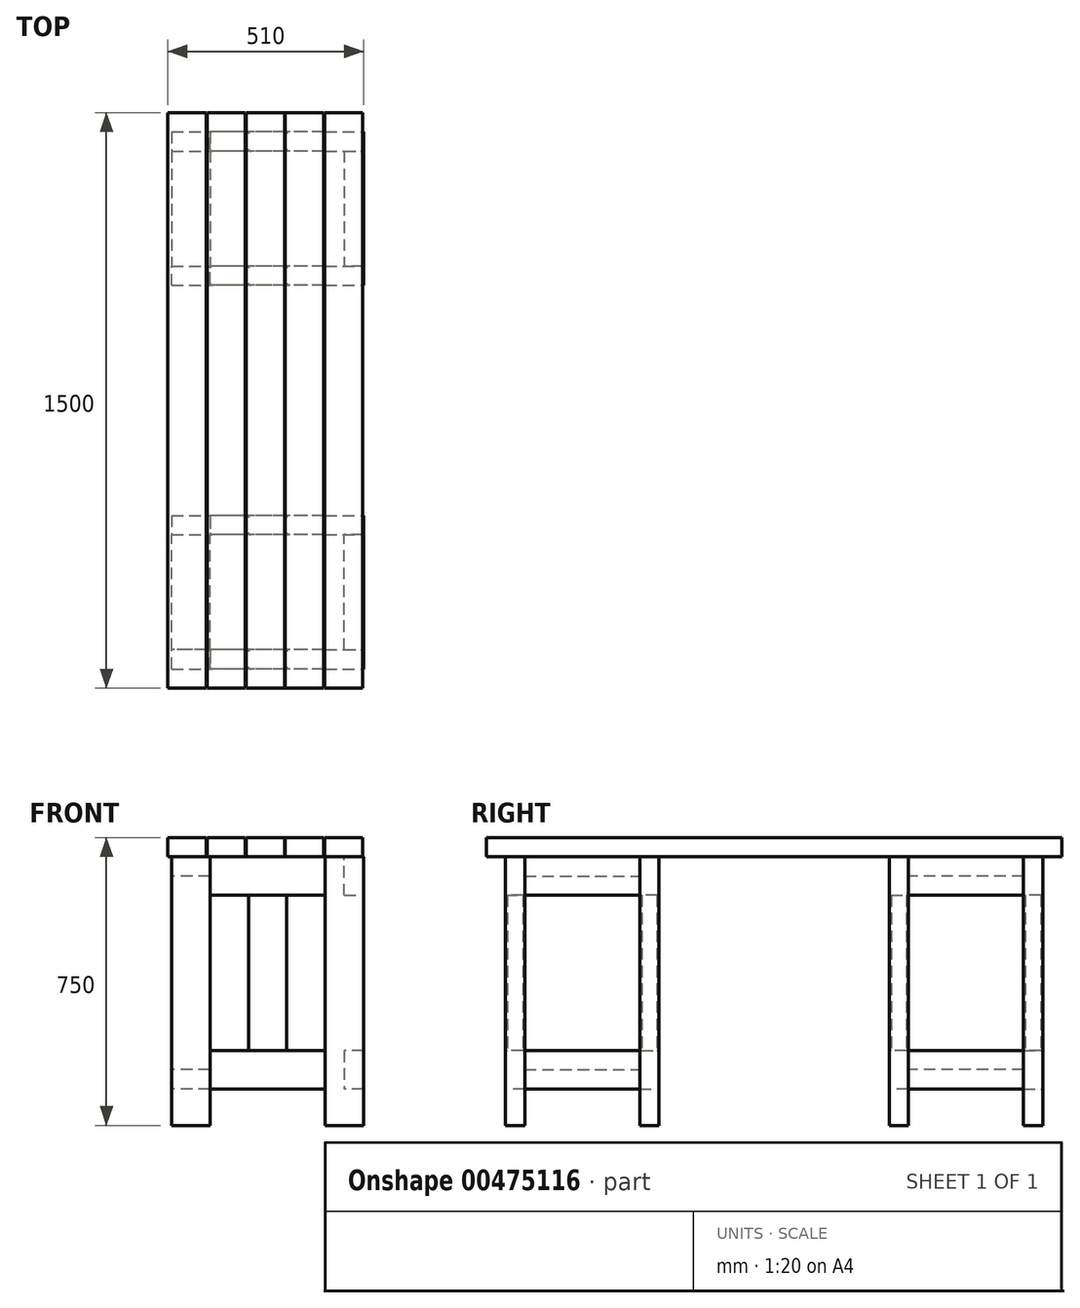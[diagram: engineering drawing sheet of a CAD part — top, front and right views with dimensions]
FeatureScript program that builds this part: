
annotation { "Feature Type Name" : "Feature", "Feature Type Description" : "" }
export const myFeature = defineFeature(function(context is Context, id is Id, definition is map)
    precondition{}
    {
        {
            var Q0;
            Q0=qCreatedBy(makeId("Top.planeOp"),FACE);
            var sketch = newSketch(context, id + "F0", { "sketchPlane" : qUnion([Q0])});
            skLineSegment(sketch, "E0.bottom", {"start": v(-98.78, -63.47) * mm, "end": v(1.22, -63.47) * mm});
            skLineSegment(sketch, "E0.top", {"start": v(-98.78, -13.47) * mm, "end": v(1.22, -13.47) * mm});
            skLineSegment(sketch, "E0.left", {"start": v(-98.78, -63.47) * mm, "end": v(-98.78, -13.47) * mm});
            skLineSegment(sketch, "E0.right", {"start": v(1.22, -63.47) * mm, "end": v(1.22, -13.47) * mm});
            skLineSegment(sketch, "E1.bottom", {"start": v(301.22, -63.47) * mm, "end": v(401.22, -63.47) * mm});
            skLineSegment(sketch, "E1.top", {"start": v(301.22, -13.47) * mm, "end": v(401.22, -13.47) * mm});
            skLineSegment(sketch, "E1.left", {"start": v(301.22, -63.47) * mm, "end": v(301.22, -13.47) * mm});
            skLineSegment(sketch, "E1.right", {"start": v(401.22, -63.47) * mm, "end": v(401.22, -13.47) * mm});
            skLineSegment(sketch, "E2.bottom", {"start": v(-98.78, 336.53) * mm, "end": v(1.22, 336.53) * mm});
            skLineSegment(sketch, "E2.top", {"start": v(-98.78, 286.53) * mm, "end": v(1.22, 286.53) * mm});
            skLineSegment(sketch, "E2.left", {"start": v(-98.78, 336.53) * mm, "end": v(-98.78, 286.53) * mm});
            skLineSegment(sketch, "E2.right", {"start": v(1.22, 336.53) * mm, "end": v(1.22, 286.53) * mm});
            skLineSegment(sketch, "E3.bottom", {"start": v(301.22, 336.53) * mm, "end": v(401.22, 336.53) * mm});
            skLineSegment(sketch, "E3.top", {"start": v(301.22, 286.53) * mm, "end": v(401.22, 286.53) * mm});
            skLineSegment(sketch, "E3.left", {"start": v(301.22, 336.53) * mm, "end": v(301.22, 286.53) * mm});
            skLineSegment(sketch, "E3.right", {"start": v(401.22, 336.53) * mm, "end": v(401.22, 286.53) * mm});
            skSolve(sketch);
        }
        {
            var Q0;
            Q0 = qSketchRegion(id + "F0", true);
            extrude(context, id + "F1", {"entities" : qUnion([Q0]), "depth" : 700 * mm, "offsetDistance" : 25 * mm});
        }
        {
            var Q0;
            Q0=makeQuery(id+"F1.opExtrude","SWEPT_FACE",FACE,{"disambiguationData":[OSD([sQuery(id+"F0.wireOp",EDGE,"E0.right")])]});
            var sketch = newSketch(context, id + "F2", { "sketchPlane" : qUnion([Q0])});
            skLineSegment(sketch, "E4.bottom", {"start": v(-13.47, 700) * mm, "end": v(-63.47, 700) * mm});
            skLineSegment(sketch, "E4.top", {"start": v(-13.47, 600) * mm, "end": v(-63.47, 600) * mm});
            skLineSegment(sketch, "E4.left", {"start": v(-13.47, 700) * mm, "end": v(-13.47, 600) * mm});
            skLineSegment(sketch, "E4.right", {"start": v(-63.47, 700) * mm, "end": v(-63.47, 600) * mm});
            skLineSegment(sketch, "E5.bottom", {"start": v(-63.47, 95) * mm, "end": v(-13.47, 95) * mm});
            skLineSegment(sketch, "E5.top", {"start": v(-63.47, 195) * mm, "end": v(-13.47, 195) * mm});
            skLineSegment(sketch, "E5.left", {"start": v(-63.47, 95) * mm, "end": v(-63.47, 195) * mm});
            skLineSegment(sketch, "E5.right", {"start": v(-13.47, 95) * mm, "end": v(-13.47, 195) * mm});
            skLineSegment(sketch, "E6.bottom", {"start": v(336.53, 700) * mm, "end": v(286.53, 700) * mm});
            skLineSegment(sketch, "E6.top", {"start": v(336.53, 600) * mm, "end": v(286.53, 600) * mm});
            skLineSegment(sketch, "E6.left", {"start": v(336.53, 700) * mm, "end": v(336.53, 600) * mm});
            skLineSegment(sketch, "E6.right", {"start": v(286.53, 700) * mm, "end": v(286.53, 600) * mm});
            skLineSegment(sketch, "E7.bottom", {"start": v(286.53, 195) * mm, "end": v(336.53, 195) * mm});
            skLineSegment(sketch, "E7.top", {"start": v(286.53, 95) * mm, "end": v(336.53, 95) * mm});
            skLineSegment(sketch, "E7.left", {"start": v(286.53, 195) * mm, "end": v(286.53, 95) * mm});
            skLineSegment(sketch, "E7.right", {"start": v(336.53, 195) * mm, "end": v(336.53, 95) * mm});
            skSolve(sketch);
        }
        {
            var Q0;
            Q0 = qSketchRegion(id + "F2", true);
            extrude(context, id + "F3", {"entities" : qUnion([Q0]), "endBound" : BoundingType.UP_TO_NEXT, "depth" : 25 * mm, "offsetDistance" : 25 * mm});
        }
        {
            var Q0;
            Q0=makeQuery(id+"F1.opExtrude","SWEPT_FACE",FACE,{"disambiguationData":[OSD([sQuery(id+"F0.wireOp",EDGE,"E2.top")])]});
            var sketch = newSketch(context, id + "F4", { "sketchPlane" : qUnion([Q0])});
            skLineSegment(sketch, "E8.bottom", {"start": v(-98.78, 700) * mm, "end": v(1.22, 700) * mm});
            skLineSegment(sketch, "E8.top", {"start": v(-98.78, 650) * mm, "end": v(1.22, 650) * mm});
            skLineSegment(sketch, "E8.left", {"start": v(-98.78, 700) * mm, "end": v(-98.78, 650) * mm});
            skLineSegment(sketch, "E8.right", {"start": v(1.22, 700) * mm, "end": v(1.22, 650) * mm});
            skLineSegment(sketch, "E9.bottom", {"start": v(-98.78, 95) * mm, "end": v(1.22, 95) * mm});
            skLineSegment(sketch, "E9.top", {"start": v(-98.78, 145) * mm, "end": v(1.22, 145) * mm});
            skLineSegment(sketch, "E9.left", {"start": v(-98.78, 95) * mm, "end": v(-98.78, 145) * mm});
            skLineSegment(sketch, "E9.right", {"start": v(1.22, 95) * mm, "end": v(1.22, 145) * mm});
            skLineSegment(sketch, "E10.bottom", {"start": v(401.22, 700) * mm, "end": v(351.22, 700) * mm});
            skLineSegment(sketch, "E10.top", {"start": v(401.22, 600) * mm, "end": v(351.22, 600) * mm});
            skLineSegment(sketch, "E10.left", {"start": v(401.22, 700) * mm, "end": v(401.22, 600) * mm});
            skLineSegment(sketch, "E10.right", {"start": v(351.22, 700) * mm, "end": v(351.22, 600) * mm});
            skLineSegment(sketch, "E11.bottom", {"start": v(351.22, 95) * mm, "end": v(401.22, 95) * mm});
            skLineSegment(sketch, "E11.top", {"start": v(351.22, 195) * mm, "end": v(401.22, 195) * mm});
            skLineSegment(sketch, "E11.left", {"start": v(351.22, 95) * mm, "end": v(351.22, 195) * mm});
            skLineSegment(sketch, "E11.right", {"start": v(401.22, 95) * mm, "end": v(401.22, 195) * mm});
            skSolve(sketch);
        }
        {
            var Q0;
            Q0 = qSketchRegion(id + "F4", true);
            extrude(context, id + "F5", {"entities" : qUnion([Q0]), "endBound" : BoundingType.UP_TO_NEXT, "depth" : 25 * mm, "offsetDistance" : 25 * mm});
        }
        {
            var Q0;
            Q0=makeQuery(id+"F3.opExtrude","SWEPT_FACE",FACE,{"disambiguationData":[OSD([sQuery(id+"F2.wireOp",EDGE,"E5.top")])]});
            var sketch = newSketch(context, id + "F6", { "sketchPlane" : qUnion([Q0])});
            skLineSegment(sketch, "E12.bottom", {"start": v(6.22, -13.47) * mm, "end": v(96.22, -13.47) * mm});
            skLineSegment(sketch, "E12.top", {"start": v(6.22, -63.47) * mm, "end": v(96.22, -63.47) * mm});
            skLineSegment(sketch, "E12.left", {"start": v(1.22, -18.47) * mm, "end": v(1.22, -58.47) * mm});
            skLineSegment(sketch, "E12.right", {"start": v(101.22, -13.47) * mm, "end": v(101.22, -63.47) * mm});
            skLineSegment(sketch, "E13.bottom", {"start": v(106.22, -13.47) * mm, "end": v(196.22, -13.47) * mm});
            skLineSegment(sketch, "E13.top", {"start": v(106.22, -63.47) * mm, "end": v(196.22, -63.47) * mm});
            skLineSegment(sketch, "E13.left", {"start": v(101.22, -18.47) * mm, "end": v(101.22, -58.47) * mm});
            skLineSegment(sketch, "E13.right", {"start": v(201.22, -13.47) * mm, "end": v(201.22, -63.47) * mm});
            skLineSegment(sketch, "E14.bottom", {"start": v(206.22, -13.47) * mm, "end": v(296.22, -13.47) * mm});
            skLineSegment(sketch, "E14.top", {"start": v(206.22, -63.47) * mm, "end": v(296.22, -63.47) * mm});
            skLineSegment(sketch, "E14.left", {"start": v(201.22, -18.47) * mm, "end": v(201.22, -58.47) * mm});
            skLineSegment(sketch, "E14.right", {"start": v(301.22, -18.47) * mm, "end": v(301.22, -58.47) * mm});
            skPoint(sketch, "E15.visualSharp", {"position": v(101.22, -63.47) * mm});
            skArc(sketch, "E15.filletArc", {"start": v(96.22, -63.47) * mm, "mid": v(99.76, -62) * mm, "end": v(101.22, -58.47) * mm});
            skPoint(sketch, "E16.visualSharp", {"position": v(101.22, -13.47) * mm});
            skArc(sketch, "E16.filletArc", {"start": v(101.22, -18.47) * mm, "mid": v(99.76, -14.94) * mm, "end": v(96.22, -13.47) * mm});
            skPoint(sketch, "E17.visualSharp", {"position": v(1.22, -13.47) * mm});
            skArc(sketch, "E17.filletArc", {"start": v(6.22, -13.47) * mm, "mid": v(2.69, -14.94) * mm, "end": v(1.22, -18.47) * mm});
            skPoint(sketch, "E18.visualSharp", {"position": v(1.22, -63.47) * mm});
            skArc(sketch, "E18.filletArc", {"start": v(1.22, -58.47) * mm, "mid": v(2.69, -62) * mm, "end": v(6.22, -63.47) * mm});
            skArc(sketch, "E19.filletArc", {"start": v(106.22, -13.47) * mm, "mid": v(102.69, -14.94) * mm, "end": v(101.22, -18.47) * mm});
            skArc(sketch, "E20.filletArc", {"start": v(101.22, -58.47) * mm, "mid": v(102.69, -62) * mm, "end": v(106.22, -63.47) * mm});
            skPoint(sketch, "E21.visualSharp", {"position": v(201.22, -63.47) * mm});
            skArc(sketch, "E21.filletArc", {"start": v(196.22, -63.47) * mm, "mid": v(199.76, -62) * mm, "end": v(201.22, -58.47) * mm});
            skPoint(sketch, "E22.visualSharp", {"position": v(201.22, -13.47) * mm});
            skArc(sketch, "E22.filletArc", {"start": v(201.22, -18.47) * mm, "mid": v(199.76, -14.94) * mm, "end": v(196.22, -13.47) * mm});
            skArc(sketch, "E23.filletArc", {"start": v(206.22, -13.47) * mm, "mid": v(202.69, -14.94) * mm, "end": v(201.22, -18.47) * mm});
            skArc(sketch, "E24.filletArc", {"start": v(201.22, -58.47) * mm, "mid": v(202.69, -62) * mm, "end": v(206.22, -63.47) * mm});
            skPoint(sketch, "E25.visualSharp", {"position": v(301.22, -13.47) * mm});
            skArc(sketch, "E25.filletArc", {"start": v(301.22, -18.47) * mm, "mid": v(299.76, -14.94) * mm, "end": v(296.22, -13.47) * mm});
            skPoint(sketch, "E26.visualSharp", {"position": v(301.22, -63.47) * mm});
            skArc(sketch, "E26.filletArc", {"start": v(296.22, -63.47) * mm, "mid": v(299.76, -62) * mm, "end": v(301.22, -58.47) * mm});
            skSolve(sketch);
        }
        {
            var Q0;
            Q0=makeQuery(id+"F6.imprint","IMPRINT",FACE,{"disambiguationData":[TD([[makeQuery(id+"F6.imprint","IMPRINT",EDGE,{"derivedFrom":sQuery(id+"F6.wireOp",EDGE,"E14.bottom")}),1.0]])]});
            var Q1;
            Q1=makeQuery(id+"F6.imprint","IMPRINT",FACE,{"disambiguationData":[TD([[makeQuery(id+"F6.imprint","IMPRINT",EDGE,{"derivedFrom":sQuery(id+"F6.wireOp",EDGE,"E13.bottom")}),1.0]])]});
            var Q2;
            Q2=makeQuery(id+"F6.imprint","IMPRINT",FACE,{"disambiguationData":[TD([[makeQuery(id+"F6.imprint","IMPRINT",EDGE,{"derivedFrom":sQuery(id+"F6.wireOp",EDGE,"E12.bottom")}),1.0]])]});
            extrude(context, id + "F7", {"entities" : qUnion([Q0, Q1, Q2]), "endBound" : BoundingType.UP_TO_NEXT, "depth" : 25 * mm, "offsetDistance" : 25 * mm});
        }
        {
            var Q0;
            Q0=makeQuery(id+"F3.opExtrude","SWEPT_FACE",FACE,{"disambiguationData":[OSD([sQuery(id+"F2.wireOp",EDGE,"E7.bottom")])]});
            var sketch = newSketch(context, id + "F8", { "sketchPlane" : qUnion([Q0])});
            skLineSegment(sketch, "E27.bottom", {"start": v(296.22, 336.53) * mm, "end": v(206.22, 336.53) * mm});
            skLineSegment(sketch, "E27.top", {"start": v(296.22, 286.53) * mm, "end": v(206.22, 286.53) * mm});
            skLineSegment(sketch, "E27.left", {"start": v(301.22, 331.53) * mm, "end": v(301.22, 291.53) * mm});
            skLineSegment(sketch, "E27.right", {"start": v(201.22, 336.53) * mm, "end": v(201.22, 286.53) * mm});
            skLineSegment(sketch, "E28.bottom", {"start": v(196.22, 336.53) * mm, "end": v(106.22, 336.53) * mm});
            skLineSegment(sketch, "E28.top", {"start": v(196.22, 286.53) * mm, "end": v(106.22, 286.53) * mm});
            skLineSegment(sketch, "E28.left", {"start": v(201.22, 331.53) * mm, "end": v(201.22, 291.53) * mm});
            skLineSegment(sketch, "E28.right", {"start": v(101.22, 336.53) * mm, "end": v(101.22, 286.53) * mm});
            skLineSegment(sketch, "E29.bottom", {"start": v(96.22, 336.53) * mm, "end": v(6.22, 336.53) * mm});
            skLineSegment(sketch, "E29.top", {"start": v(96.22, 286.53) * mm, "end": v(6.22, 286.53) * mm});
            skLineSegment(sketch, "E29.left", {"start": v(101.22, 331.53) * mm, "end": v(101.22, 291.53) * mm});
            skLineSegment(sketch, "E29.right", {"start": v(1.22, 331.53) * mm, "end": v(1.22, 291.53) * mm});
            skPoint(sketch, "E30.visualSharp", {"position": v(301.22, 286.53) * mm});
            skArc(sketch, "E30.filletArc", {"start": v(296.22, 286.53) * mm, "mid": v(299.76, 288) * mm, "end": v(301.22, 291.53) * mm});
            skPoint(sketch, "E31.visualSharp", {"position": v(301.22, 336.53) * mm});
            skArc(sketch, "E31.filletArc", {"start": v(301.22, 331.53) * mm, "mid": v(299.76, 335.06) * mm, "end": v(296.22, 336.53) * mm});
            skPoint(sketch, "E32.visualSharp", {"position": v(201.22, 336.53) * mm});
            skArc(sketch, "E32.filletArc", {"start": v(206.22, 336.53) * mm, "mid": v(202.69, 335.06) * mm, "end": v(201.22, 331.53) * mm});
            skPoint(sketch, "E33.visualSharp", {"position": v(201.22, 286.53) * mm});
            skArc(sketch, "E33.filletArc", {"start": v(201.22, 291.53) * mm, "mid": v(202.69, 288) * mm, "end": v(206.22, 286.53) * mm});
            skArc(sketch, "E34.filletArc", {"start": v(196.22, 286.53) * mm, "mid": v(199.76, 288) * mm, "end": v(201.22, 291.53) * mm});
            skArc(sketch, "E35.filletArc", {"start": v(201.22, 331.53) * mm, "mid": v(199.76, 335.06) * mm, "end": v(196.22, 336.53) * mm});
            skPoint(sketch, "E36.visualSharp", {"position": v(101.22, 286.53) * mm});
            skArc(sketch, "E36.filletArc", {"start": v(101.22, 291.53) * mm, "mid": v(102.69, 288) * mm, "end": v(106.22, 286.53) * mm});
            skPoint(sketch, "E37.visualSharp", {"position": v(101.22, 336.53) * mm});
            skArc(sketch, "E37.filletArc", {"start": v(106.22, 336.53) * mm, "mid": v(102.69, 335.06) * mm, "end": v(101.22, 331.53) * mm});
            skArc(sketch, "E38.filletArc", {"start": v(101.22, 331.53) * mm, "mid": v(99.76, 335.06) * mm, "end": v(96.22, 336.53) * mm});
            skArc(sketch, "E39.filletArc", {"start": v(96.22, 286.53) * mm, "mid": v(99.76, 288) * mm, "end": v(101.22, 291.53) * mm});
            skPoint(sketch, "E40.visualSharp", {"position": v(1.22, 336.53) * mm});
            skArc(sketch, "E40.filletArc", {"start": v(6.22, 336.53) * mm, "mid": v(2.69, 335.06) * mm, "end": v(1.22, 331.53) * mm});
            skPoint(sketch, "E41.visualSharp", {"position": v(1.22, 286.53) * mm});
            skArc(sketch, "E41.filletArc", {"start": v(1.22, 291.53) * mm, "mid": v(2.69, 288) * mm, "end": v(6.22, 286.53) * mm});
            skSolve(sketch);
        }
        {
            var Q0;
            Q0 = qSketchRegion(id + "F8", true);
            extrude(context, id + "F9", {"entities" : qUnion([Q0]), "endBound" : BoundingType.UP_TO_NEXT, "depth" : 25 * mm, "offsetDistance" : 25 * mm});
        }
        {
            var Q0;
            Q0=makeQuery(id+"F1.opExtrude","CAP_FACE",FACE,{"disambiguationData":[OSD([sQuery(id+"F0.wireOp",EDGE,"E0.bottom"),sQuery(id+"F0.wireOp",EDGE,"E0.top"),sQuery(id+"F0.wireOp",EDGE,"E0.left"),sQuery(id+"F0.wireOp",EDGE,"E0.right")])],"isStart":false});
            var sketch = newSketch(context, id + "F10", { "sketchPlane" : qUnion([Q0])});
            skLineSegment(sketch, "E42.bottom", {"start": v(399.22, -113.47) * mm, "end": v(299.22, -113.47) * mm});
            skLineSegment(sketch, "E42.top", {"start": v(399.22, 1386.53) * mm, "end": v(299.22, 1386.53) * mm});
            skLineSegment(sketch, "E42.left", {"start": v(399.22, -113.47) * mm, "end": v(399.22, 1386.53) * mm});
            skLineSegment(sketch, "E42.right", {"start": v(299.22, -113.47) * mm, "end": v(299.22, 1386.53) * mm});
            skLineSegment(sketch, "E43.bottom", {"start": v(297.22, -113.47) * mm, "end": v(197.22, -113.47) * mm});
            skLineSegment(sketch, "E43.top", {"start": v(297.22, 1386.53) * mm, "end": v(197.22, 1386.53) * mm});
            skLineSegment(sketch, "E43.left", {"start": v(297.22, -113.47) * mm, "end": v(297.22, 1386.53) * mm});
            skLineSegment(sketch, "E43.right", {"start": v(197.22, -113.47) * mm, "end": v(197.22, 1386.53) * mm});
            skLineSegment(sketch, "E44.bottom", {"start": v(195.22, -113.47) * mm, "end": v(95.22, -113.47) * mm});
            skLineSegment(sketch, "E44.top", {"start": v(195.22, 1386.53) * mm, "end": v(95.22, 1386.53) * mm});
            skLineSegment(sketch, "E44.left", {"start": v(195.22, -113.47) * mm, "end": v(195.22, 1386.53) * mm});
            skLineSegment(sketch, "E44.right", {"start": v(95.22, -113.47) * mm, "end": v(95.22, 1386.53) * mm});
            skLineSegment(sketch, "E45.bottom", {"start": v(93.22, -113.47) * mm, "end": v(-6.78, -113.47) * mm});
            skLineSegment(sketch, "E45.top", {"start": v(93.22, 1386.53) * mm, "end": v(-6.78, 1386.53) * mm});
            skLineSegment(sketch, "E45.left", {"start": v(93.22, -113.47) * mm, "end": v(93.22, 1386.53) * mm});
            skLineSegment(sketch, "E45.right", {"start": v(-6.78, -113.47) * mm, "end": v(-6.78, 1386.53) * mm});
            skLineSegment(sketch, "E46.bottom", {"start": v(-8.78, -113.47) * mm, "end": v(-108.78, -113.47) * mm});
            skLineSegment(sketch, "E46.top", {"start": v(-8.78, 1386.53) * mm, "end": v(-108.78, 1386.53) * mm});
            skLineSegment(sketch, "E46.left", {"start": v(-8.78, -113.47) * mm, "end": v(-8.78, 1386.53) * mm});
            skLineSegment(sketch, "E46.right", {"start": v(-108.78, -113.47) * mm, "end": v(-108.78, 1386.53) * mm});
            skSolve(sketch);
        }
        {
            var Q0;
            Q0 = qSketchRegion(id + "F10", true);
            extrude(context, id + "F11", {"entities" : qUnion([Q0]), "depth" : 50 * mm, "offsetDistance" : 25 * mm});
        }
        {
            var Q0;
            Q0=makeQuery(id+"F3.opExtrude","SWEPT_FACE",FACE,{"disambiguationData":[OSD([sQuery(id+"F2.wireOp",EDGE,"E6.left")])]});
            cPlane(context, id + "F12", {"entities" : qUnion([Q0]), "cplaneType" : CPlaneType.OFFSET, "offset" : 300 * mm, "width" : 150 * mm, "height" : 150 * mm});
        }
        {
            var Q0;
            Q0=makeQuery(id+"F3.opExtrude","SWEPT_BODY",BODY,{"disambiguationData":[OSD([sQuery(id+"F2.wireOp",EDGE,"E6.bottom"),sQuery(id+"F2.wireOp",EDGE,"E6.top"),sQuery(id+"F2.wireOp",EDGE,"E6.left"),sQuery(id+"F2.wireOp",EDGE,"E6.right")])]});
            var Q1;
            Q1=makeQuery(id+"F1.opExtrude","SWEPT_BODY",BODY,{"disambiguationData":[OSD([sQuery(id+"F0.wireOp",EDGE,"E2.bottom"),sQuery(id+"F0.wireOp",EDGE,"E2.top"),sQuery(id+"F0.wireOp",EDGE,"E2.left"),sQuery(id+"F0.wireOp",EDGE,"E2.right")])]});
            var Q2;
            Q2=makeQuery(id+"F9.opExtrude","SWEPT_BODY",BODY,{"disambiguationData":[OSD([sQuery(id+"F8.wireOp",EDGE,"E27.bottom"),sQuery(id+"F8.wireOp",EDGE,"E27.top"),sQuery(id+"F8.wireOp",EDGE,"E27.left"),sQuery(id+"F8.wireOp",EDGE,"E28.bottom"),sQuery(id+"F8.wireOp",EDGE,"E28.top"),sQuery(id+"F8.wireOp",EDGE,"E29.bottom"),sQuery(id+"F8.wireOp",EDGE,"E29.top"),sQuery(id+"F8.wireOp",EDGE,"E29.right"),sQuery(id+"F8.wireOp",EDGE,"E30.filletArc"),sQuery(id+"F8.wireOp",EDGE,"E31.filletArc"),sQuery(id+"F8.wireOp",EDGE,"E32.filletArc"),sQuery(id+"F8.wireOp",EDGE,"E33.filletArc"),sQuery(id+"F8.wireOp",EDGE,"E34.filletArc"),sQuery(id+"F8.wireOp",EDGE,"E35.filletArc"),sQuery(id+"F8.wireOp",EDGE,"E36.filletArc"),sQuery(id+"F8.wireOp",EDGE,"E37.filletArc"),sQuery(id+"F8.wireOp",EDGE,"E38.filletArc"),sQuery(id+"F8.wireOp",EDGE,"E39.filletArc"),sQuery(id+"F8.wireOp",EDGE,"E40.filletArc"),sQuery(id+"F8.wireOp",EDGE,"E41.filletArc")])]});
            var Q3;
            Q3=makeQuery(id+"F1.opExtrude","SWEPT_BODY",BODY,{"disambiguationData":[OSD([sQuery(id+"F0.wireOp",EDGE,"E3.bottom"),sQuery(id+"F0.wireOp",EDGE,"E3.top"),sQuery(id+"F0.wireOp",EDGE,"E3.left"),sQuery(id+"F0.wireOp",EDGE,"E3.right")])]});
            var Q4;
            Q4=makeQuery(id+"F3.opExtrude","SWEPT_BODY",BODY,{"disambiguationData":[OSD([sQuery(id+"F2.wireOp",EDGE,"E7.bottom"),sQuery(id+"F2.wireOp",EDGE,"E7.top"),sQuery(id+"F2.wireOp",EDGE,"E7.left"),sQuery(id+"F2.wireOp",EDGE,"E7.right")])]});
            var Q5;
            Q5=makeQuery(id+"F1.opExtrude","SWEPT_BODY",BODY,{"disambiguationData":[OSD([sQuery(id+"F0.wireOp",EDGE,"E0.bottom"),sQuery(id+"F0.wireOp",EDGE,"E0.top"),sQuery(id+"F0.wireOp",EDGE,"E0.left"),sQuery(id+"F0.wireOp",EDGE,"E0.right")])]});
            var Q6;
            Q6=makeQuery(id+"F1.opExtrude","SWEPT_BODY",BODY,{"disambiguationData":[OSD([sQuery(id+"F0.wireOp",EDGE,"E1.bottom"),sQuery(id+"F0.wireOp",EDGE,"E1.top"),sQuery(id+"F0.wireOp",EDGE,"E1.left"),sQuery(id+"F0.wireOp",EDGE,"E1.right")])]});
            var Q7;
            Q7=makeQuery(id+"F3.opExtrude","SWEPT_BODY",BODY,{"disambiguationData":[OSD([sQuery(id+"F2.wireOp",EDGE,"E4.bottom"),sQuery(id+"F2.wireOp",EDGE,"E4.top"),sQuery(id+"F2.wireOp",EDGE,"E4.left"),sQuery(id+"F2.wireOp",EDGE,"E4.right")])]});
            var Q8;
            Q8=makeQuery(id+"F3.opExtrude","SWEPT_BODY",BODY,{"disambiguationData":[OSD([sQuery(id+"F2.wireOp",EDGE,"E5.bottom"),sQuery(id+"F2.wireOp",EDGE,"E5.top"),sQuery(id+"F2.wireOp",EDGE,"E5.left"),sQuery(id+"F2.wireOp",EDGE,"E5.right")])]});
            var Q9;
            Q9=makeQuery(id+"F5.opExtrude","SWEPT_BODY",BODY,{"disambiguationData":[OSD([sQuery(id+"F4.wireOp",EDGE,"E8.bottom"),sQuery(id+"F4.wireOp",EDGE,"E8.top"),sQuery(id+"F4.wireOp",EDGE,"E8.left"),sQuery(id+"F4.wireOp",EDGE,"E8.right")])]});
            var Q10;
            Q10=makeQuery(id+"F5.opExtrude","SWEPT_BODY",BODY,{"disambiguationData":[OSD([sQuery(id+"F4.wireOp",EDGE,"E9.bottom"),sQuery(id+"F4.wireOp",EDGE,"E9.top"),sQuery(id+"F4.wireOp",EDGE,"E9.left"),sQuery(id+"F4.wireOp",EDGE,"E9.right")])]});
            var Q11;
            Q11=makeQuery(id+"F5.opExtrude","SWEPT_BODY",BODY,{"disambiguationData":[OSD([sQuery(id+"F4.wireOp",EDGE,"E10.bottom"),sQuery(id+"F4.wireOp",EDGE,"E10.top"),sQuery(id+"F4.wireOp",EDGE,"E10.left"),sQuery(id+"F4.wireOp",EDGE,"E10.right")])]});
            var Q12;
            Q12=makeQuery(id+"F5.opExtrude","SWEPT_BODY",BODY,{"disambiguationData":[OSD([sQuery(id+"F4.wireOp",EDGE,"E11.bottom"),sQuery(id+"F4.wireOp",EDGE,"E11.top"),sQuery(id+"F4.wireOp",EDGE,"E11.left"),sQuery(id+"F4.wireOp",EDGE,"E11.right")])]});
            var Q13;
            Q13=makeQuery(id+"F7.opExtrude","SWEPT_BODY",BODY,{"disambiguationData":[OSD([sQuery(id+"F6.wireOp",EDGE,"E12.bottom"),sQuery(id+"F6.wireOp",EDGE,"E12.top"),sQuery(id+"F6.wireOp",EDGE,"E12.left"),sQuery(id+"F6.wireOp",EDGE,"E13.bottom"),sQuery(id+"F6.wireOp",EDGE,"E13.top"),sQuery(id+"F6.wireOp",EDGE,"E14.bottom"),sQuery(id+"F6.wireOp",EDGE,"E14.top"),sQuery(id+"F6.wireOp",EDGE,"E14.right"),sQuery(id+"F6.wireOp",EDGE,"E15.filletArc"),sQuery(id+"F6.wireOp",EDGE,"E16.filletArc"),sQuery(id+"F6.wireOp",EDGE,"E17.filletArc"),sQuery(id+"F6.wireOp",EDGE,"E18.filletArc"),sQuery(id+"F6.wireOp",EDGE,"E19.filletArc"),sQuery(id+"F6.wireOp",EDGE,"E20.filletArc"),sQuery(id+"F6.wireOp",EDGE,"E21.filletArc"),sQuery(id+"F6.wireOp",EDGE,"E22.filletArc"),sQuery(id+"F6.wireOp",EDGE,"E23.filletArc"),sQuery(id+"F6.wireOp",EDGE,"E24.filletArc"),sQuery(id+"F6.wireOp",EDGE,"E25.filletArc"),sQuery(id+"F6.wireOp",EDGE,"E26.filletArc")])]});
            var Q14;
            Q14=qCreatedBy(id+"F12.planeOp",FACE);
            mirror(context, id + "F13", {"entities" : qUnion([Q0, Q1, Q2, Q3, Q4, Q5, Q6, Q7, Q8, Q9, Q10, Q11, Q12, Q13]), "mirrorPlane" : qUnion([Q14])});
        }
    });
